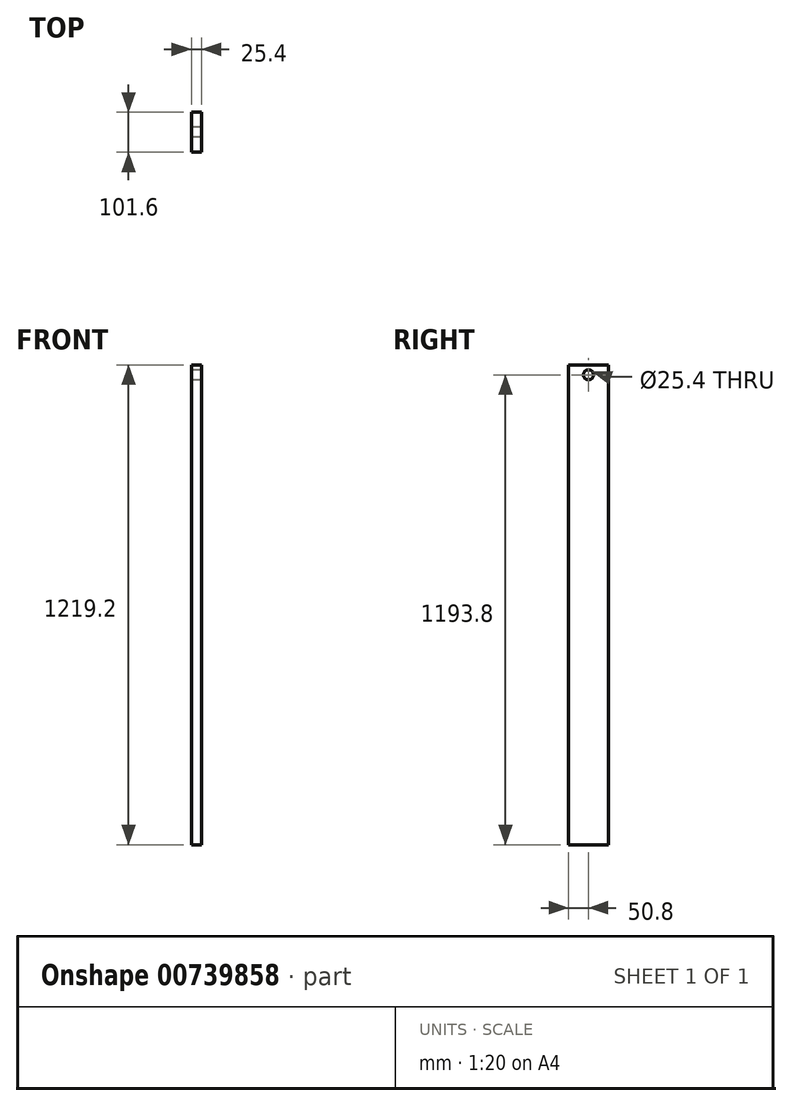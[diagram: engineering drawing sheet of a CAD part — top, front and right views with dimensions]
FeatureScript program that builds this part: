
annotation { "Feature Type Name" : "Feature", "Feature Type Description" : "" }
export const myFeature = defineFeature(function(context is Context, id is Id, definition is map)
    precondition{}
    {
        {
            var Q0;
            Q0=qCreatedBy(makeId("Right.planeOp"),FACE);
            var sketch = newSketch(context, id + "F0", { "sketchPlane" : qUnion([Q0])});
            skLineSegment(sketch, "E0.bottom", {"start": v(0, 0) * mm, "end": v(-50.8, 0) * mm});
            skLineSegment(sketch, "E0.top", {"start": v(0, 0) * mm, "end": v(-50.8, 0) * mm});
            skLineSegment(sketch, "E0.left", {"start": v(0, 0) * mm, "end": v(0, 0) * mm});
            skLineSegment(sketch, "E0.right", {"start": v(-50.8, 0) * mm, "end": v(-50.8, 0) * mm});
            skLineSegment(sketch, "E1.bottom", {"start": v(0, 0) * mm, "end": v(50.8, 0) * mm});
            skLineSegment(sketch, "E1.top", {"start": v(0, 0) * mm, "end": v(50.8, 0) * mm});
            skLineSegment(sketch, "E1.right", {"start": v(50.8, 0) * mm, "end": v(50.8, 0) * mm});
            skLineSegment(sketch, "E2", {"start": v(50.8, 0) * mm, "end": v(50.8, -1219.2) * mm});
            skLineSegment(sketch, "E3", {"start": v(50.8, -1219.2) * mm, "end": v(-50.8, -1219.2) * mm});
            skLineSegment(sketch, "E4", {"start": v(-50.8, -1219.2) * mm, "end": v(-50.8, 0) * mm});
            skLineSegment(sketch, "E5", {"start": v(0, 0) * mm, "end": v(0, -25.4) * mm});
            skCircle(sketch, "E6", {"center": v(0, -25.4) * mm, "radius": 12.7 * mm});
            skSolve(sketch);
        }
        {
            var Q0;
            Q0 = qSketchRegion(id + "F0", true);
            extrude(context, id + "F1", {"entities" : qUnion([Q0]), "depth" : 25.4 * mm, "offsetDistance" : 25.4 * mm});
        }
    });
